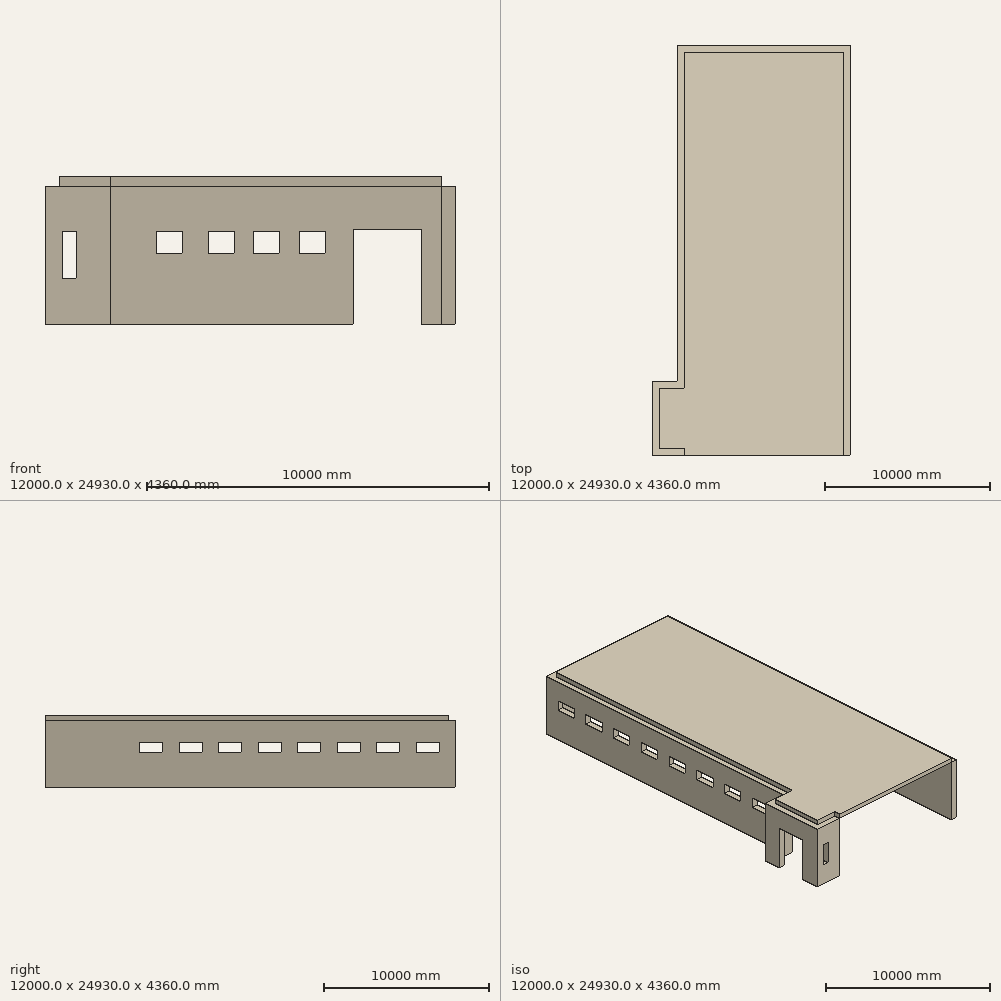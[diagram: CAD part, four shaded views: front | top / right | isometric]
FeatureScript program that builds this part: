
annotation { "Feature Type Name" : "Feature", "Feature Type Description" : "" }
export const myFeature = defineFeature(function(context is Context, id is Id, definition is map)
    precondition{}
    {
        {
            var Q0;
            Q0=qCreatedBy(makeId("Top.planeOp"),FACE);
            var sketch = newSketch(context, id + "F0", { "sketchPlane" : qUnion([Q0])});
            skLineSegment(sketch, "E0", {"start": v(0, 0) * mm, "end": v(0, 24930) * mm});
            skLineSegment(sketch, "E1", {"start": v(0, 24930) * mm, "end": v(-10500, 24930) * mm});
            skLineSegment(sketch, "E2", {"start": v(-10500, 24930) * mm, "end": v(-10500, 4500) * mm});
            skLineSegment(sketch, "E3", {"start": v(-10500, 4500) * mm, "end": v(-12000, 4500) * mm});
            skLineSegment(sketch, "E4", {"start": v(-12000, 4500) * mm, "end": v(-12000, 0) * mm});
            skLineSegment(sketch, "E5.0", {"start": v(-11585, 4085) * mm, "end": v(-11585, 415) * mm});
            skLineSegment(sketch, "E5.1", {"start": v(-10085, 4085) * mm, "end": v(-11585, 4085) * mm});
            skLineSegment(sketch, "E5.2", {"start": v(-10085, 24515) * mm, "end": v(-10085, 4085) * mm});
            skLineSegment(sketch, "E5.3", {"start": v(-415, 24515) * mm, "end": v(-10085, 24515) * mm});
            skLineSegment(sketch, "E5.4", {"start": v(-415, 0) * mm, "end": v(-415, 24515) * mm});
            skLineSegment(sketch, "E6", {"start": v(-12000, 0) * mm, "end": v(-10085, 0) * mm});
            skLineSegment(sketch, "E7", {"start": v(-11585, 415) * mm, "end": v(-10085, 415) * mm});
            skLineSegment(sketch, "E8", {"start": v(-10085, 415) * mm, "end": v(-10085, 0) * mm});
            skLineSegment(sketch, "E9", {"start": v(-415, 0) * mm, "end": v(0, 0) * mm});
            skSolve(sketch);
        }
        {
            var Q0;
            Q0 = qSketchRegion(id + "F0", true);
            extrude(context, id + "F1", {"entities" : qUnion([Q0]), "depth" : 4060 * mm});
        }
        {
            var Q0;
            Q0=makeQuery(id+"F1.opExtrude","SWEPT_FACE",FACE,{"disambiguationData":[OSD([sQuery(id+"F0.wireOp",EDGE,"E2")])]});
            var sketch = newSketch(context, id + "F2", { "sketchPlane" : qUnion([Q0])});
            skLineSegment(sketch, "E10.rect.bottom", {"start": v(-22530, 2100) * mm, "end": v(-23930, 2100) * mm});
            skLineSegment(sketch, "E10.rect.top", {"start": v(-22530, 2750) * mm, "end": v(-23930, 2750) * mm});
            skLineSegment(sketch, "E10.rect.left", {"start": v(-22530, 2100) * mm, "end": v(-22530, 2750) * mm});
            skLineSegment(sketch, "E10.rect.right", {"start": v(-23930, 2100) * mm, "end": v(-23930, 2750) * mm});
            skPoint(sketch, "E10.rect.middle", {"position": v(-23230, 2425) * mm});
            skLineSegment(sketch, "E11.rect.bottom", {"start": v(-20130, 2100) * mm, "end": v(-21530, 2100) * mm});
            skLineSegment(sketch, "E11.rect.top", {"start": v(-20130, 2750) * mm, "end": v(-21530, 2750) * mm});
            skLineSegment(sketch, "E11.rect.left", {"start": v(-20130, 2100) * mm, "end": v(-20130, 2750) * mm});
            skLineSegment(sketch, "E11.rect.right", {"start": v(-21530, 2100) * mm, "end": v(-21530, 2750) * mm});
            skPoint(sketch, "E11.rect.middle", {"position": v(-20830, 2425) * mm});
            skLineSegment(sketch, "E12.rect.bottom", {"start": v(-17730, 2100) * mm, "end": v(-19130, 2100) * mm});
            skLineSegment(sketch, "E12.rect.top", {"start": v(-17730, 2750) * mm, "end": v(-19130, 2750) * mm});
            skLineSegment(sketch, "E12.rect.left", {"start": v(-17730, 2100) * mm, "end": v(-17730, 2750) * mm});
            skLineSegment(sketch, "E12.rect.right", {"start": v(-19130, 2100) * mm, "end": v(-19130, 2750) * mm});
            skPoint(sketch, "E12.rect.middle", {"position": v(-18430, 2425) * mm});
            skLineSegment(sketch, "E13.rect.bottom", {"start": v(-15330, 2100) * mm, "end": v(-16730, 2100) * mm});
            skLineSegment(sketch, "E13.rect.top", {"start": v(-15330, 2750) * mm, "end": v(-16730, 2750) * mm});
            skLineSegment(sketch, "E13.rect.left", {"start": v(-15330, 2100) * mm, "end": v(-15330, 2750) * mm});
            skLineSegment(sketch, "E13.rect.right", {"start": v(-16730, 2100) * mm, "end": v(-16730, 2750) * mm});
            skPoint(sketch, "E13.rect.middle", {"position": v(-16030, 2425) * mm});
            skLineSegment(sketch, "E14.rect.bottom", {"start": v(-12930, 2100) * mm, "end": v(-14330, 2100) * mm});
            skLineSegment(sketch, "E14.rect.top", {"start": v(-12930, 2750) * mm, "end": v(-14330, 2750) * mm});
            skLineSegment(sketch, "E14.rect.left", {"start": v(-12930, 2100) * mm, "end": v(-12930, 2750) * mm});
            skLineSegment(sketch, "E14.rect.right", {"start": v(-14330, 2100) * mm, "end": v(-14330, 2750) * mm});
            skPoint(sketch, "E14.rect.middle", {"position": v(-13630, 2425) * mm});
            skLineSegment(sketch, "E15.rect.bottom", {"start": v(-10530, 2100) * mm, "end": v(-11930, 2100) * mm});
            skLineSegment(sketch, "E15.rect.top", {"start": v(-10530, 2750) * mm, "end": v(-11930, 2750) * mm});
            skLineSegment(sketch, "E15.rect.left", {"start": v(-10530, 2100) * mm, "end": v(-10530, 2750) * mm});
            skLineSegment(sketch, "E15.rect.right", {"start": v(-11930, 2100) * mm, "end": v(-11930, 2750) * mm});
            skPoint(sketch, "E15.rect.middle", {"position": v(-11230, 2425) * mm});
            skLineSegment(sketch, "E16.rect.bottom", {"start": v(-8130, 2100) * mm, "end": v(-9530, 2100) * mm});
            skLineSegment(sketch, "E16.rect.top", {"start": v(-8130, 2750) * mm, "end": v(-9530, 2750) * mm});
            skLineSegment(sketch, "E16.rect.left", {"start": v(-8130, 2100) * mm, "end": v(-8130, 2750) * mm});
            skLineSegment(sketch, "E16.rect.right", {"start": v(-9530, 2100) * mm, "end": v(-9530, 2750) * mm});
            skPoint(sketch, "E16.rect.middle", {"position": v(-8830, 2425) * mm});
            skLineSegment(sketch, "E17.rect.bottom", {"start": v(-5730, 2100) * mm, "end": v(-7130, 2100) * mm});
            skLineSegment(sketch, "E17.rect.top", {"start": v(-5730, 2750) * mm, "end": v(-7130, 2750) * mm});
            skLineSegment(sketch, "E17.rect.left", {"start": v(-5730, 2100) * mm, "end": v(-5730, 2750) * mm});
            skLineSegment(sketch, "E17.rect.right", {"start": v(-7130, 2100) * mm, "end": v(-7130, 2750) * mm});
            skPoint(sketch, "E17.rect.middle", {"position": v(-6430, 2425) * mm});
            skSolve(sketch);
        }
        {
            var Q0;
            Q0 = qSketchRegion(id + "F2", true);
            extrude(context, id + "F3", {"entities" : qUnion([Q0]), "operationType" : NewBodyOperationType.REMOVE, "endBound" : BoundingType.THROUGH_ALL, "oppositeDirection" : true, "depth" : 5000 * mm});
        }
        {
            var Q0;
            Q0=makeQuery(id+"F1.opExtrude","SWEPT_FACE",FACE,{"disambiguationData":[OSD([sQuery(id+"F0.wireOp",EDGE,"E6")])]});
            var sketch = newSketch(context, id + "F4", { "sketchPlane" : qUnion([Q0])});
            skLineSegment(sketch, "E18.rect.bottom", {"start": v(-11100, 1350) * mm, "end": v(-11500, 1350) * mm});
            skLineSegment(sketch, "E18.rect.top", {"start": v(-11100, 2750) * mm, "end": v(-11500, 2750) * mm});
            skLineSegment(sketch, "E18.rect.left", {"start": v(-11100, 1350) * mm, "end": v(-11100, 2750) * mm});
            skLineSegment(sketch, "E18.rect.right", {"start": v(-11500, 1350) * mm, "end": v(-11500, 2750) * mm});
            skPoint(sketch, "E18.rect.middle", {"position": v(-11300, 2050) * mm});
            skSolve(sketch);
        }
        {
            var Q0;
            Q0 = qSketchRegion(id + "F4", true);
            extrude(context, id + "F5", {"entities" : qUnion([Q0]), "operationType" : NewBodyOperationType.REMOVE, "endBound" : BoundingType.THROUGH_ALL, "oppositeDirection" : true, "depth" : 25 * mm});
        }
        {
            var Q0;
            Q0=makeQuery(id+"F1.opExtrude","SWEPT_FACE",FACE,{"disambiguationData":[OSD([sQuery(id+"F0.wireOp",EDGE,"E1")])]});
            var sketch = newSketch(context, id + "F6", { "sketchPlane" : qUnion([Q0])});
            skLineSegment(sketch, "E19.bottom", {"start": v(8754.62, 2100) * mm, "end": v(7994.62, 2100) * mm});
            skLineSegment(sketch, "E19.top", {"start": v(8754.62, 2750) * mm, "end": v(7994.62, 2750) * mm});
            skLineSegment(sketch, "E19.left", {"start": v(8754.62, 2100) * mm, "end": v(8754.62, 2750) * mm});
            skLineSegment(sketch, "E19.right", {"start": v(7994.62, 2100) * mm, "end": v(7994.62, 2750) * mm});
            skLineSegment(sketch, "E20.bottom", {"start": v(7234.62, 2100) * mm, "end": v(6474.62, 2100) * mm});
            skLineSegment(sketch, "E20.top", {"start": v(7234.62, 2750) * mm, "end": v(6474.62, 2750) * mm});
            skLineSegment(sketch, "E20.left", {"start": v(7234.62, 2100) * mm, "end": v(7234.62, 2750) * mm});
            skLineSegment(sketch, "E20.right", {"start": v(6474.62, 2100) * mm, "end": v(6474.62, 2750) * mm});
            skLineSegment(sketch, "E21.bottom", {"start": v(5916.25, 2100) * mm, "end": v(5156.25, 2100) * mm});
            skLineSegment(sketch, "E21.top", {"start": v(5916.25, 2750) * mm, "end": v(5156.25, 2750) * mm});
            skLineSegment(sketch, "E21.left", {"start": v(5916.25, 2100) * mm, "end": v(5916.25, 2750) * mm});
            skLineSegment(sketch, "E21.right", {"start": v(5156.25, 2100) * mm, "end": v(5156.25, 2750) * mm});
            skLineSegment(sketch, "E22.bottom", {"start": v(4551.35, 2100) * mm, "end": v(3791.35, 2100) * mm});
            skLineSegment(sketch, "E22.top", {"start": v(4551.35, 2750) * mm, "end": v(3791.35, 2750) * mm});
            skLineSegment(sketch, "E22.left", {"start": v(4551.35, 2100) * mm, "end": v(4551.35, 2750) * mm});
            skLineSegment(sketch, "E22.right", {"start": v(3791.35, 2100) * mm, "end": v(3791.35, 2750) * mm});
            skLineSegment(sketch, "E23.bottom", {"start": v(2999.51, 0) * mm, "end": v(999.51, 0) * mm});
            skLineSegment(sketch, "E23.top", {"start": v(2999.51, 2800) * mm, "end": v(999.51, 2800) * mm});
            skLineSegment(sketch, "E23.left", {"start": v(2999.51, 0) * mm, "end": v(2999.51, 2800) * mm});
            skLineSegment(sketch, "E23.right", {"start": v(999.51, 0) * mm, "end": v(999.51, 2800) * mm});
            skSolve(sketch);
        }
        {
            var Q0;
            Q0=makeQuery(id+"F6.imprint","IMPRINT",FACE,{"disambiguationData":[TD([[makeQuery(id+"F6.imprint","IMPRINT",EDGE,{"derivedFrom":sQuery(id+"F6.wireOp",EDGE,"E23.bottom")}),1.0]])]});
            var Q1;
            Q1=makeQuery(id+"F6.imprint","IMPRINT",FACE,{"disambiguationData":[TD([[makeQuery(id+"F6.imprint","IMPRINT",EDGE,{"derivedFrom":sQuery(id+"F6.wireOp",EDGE,"E22.bottom")}),-1.0]])]});
            var Q2;
            Q2=makeQuery(id+"F6.imprint","IMPRINT",FACE,{"disambiguationData":[TD([[makeQuery(id+"F6.imprint","IMPRINT",EDGE,{"derivedFrom":sQuery(id+"F6.wireOp",EDGE,"E21.bottom")}),-1.0]])]});
            var Q3;
            Q3=makeQuery(id+"F6.imprint","IMPRINT",FACE,{"disambiguationData":[TD([[makeQuery(id+"F6.imprint","IMPRINT",EDGE,{"derivedFrom":sQuery(id+"F6.wireOp",EDGE,"E20.bottom")}),-1.0]])]});
            var Q4;
            Q4=makeQuery(id+"F6.imprint","IMPRINT",FACE,{"disambiguationData":[TD([[makeQuery(id+"F6.imprint","IMPRINT",EDGE,{"derivedFrom":sQuery(id+"F6.wireOp",EDGE,"E19.bottom")}),-1.0]])]});
            extrude(context, id + "F7", {"entities" : qUnion([Q0, Q1, Q2, Q3, Q4]), "operationType" : NewBodyOperationType.REMOVE, "endBound" : BoundingType.THROUGH_ALL, "oppositeDirection" : true, "depth" : 25 * mm});
        }
        {
            var Q0;
            Q0=makeQuery(id+"F1.opExtrude","SWEPT_FACE",FACE,{"disambiguationData":[OSD([sQuery(id+"F0.wireOp",EDGE,"E4")])]});
            var sketch = newSketch(context, id + "F8", { "sketchPlane" : qUnion([Q0])});
            skLineSegment(sketch, "E24.bottom", {"start": v(-1300, 0) * mm, "end": v(-3300, 0) * mm});
            skLineSegment(sketch, "E24.top", {"start": v(-1300, 2800) * mm, "end": v(-3300, 2800) * mm});
            skLineSegment(sketch, "E24.left", {"start": v(-1300, 0) * mm, "end": v(-1300, 2800) * mm});
            skLineSegment(sketch, "E24.right", {"start": v(-3300, 0) * mm, "end": v(-3300, 2800) * mm});
            skSolve(sketch);
        }
        {
            var Q0;
            Q0=makeQuery(id+"F8.imprint","IMPRINT",FACE,{"disambiguationData":[TD([[makeQuery(id+"F8.imprint","IMPRINT",EDGE,{"derivedFrom":sQuery(id+"F8.wireOp",EDGE,"E24.bottom")}),1.0]])]});
            extrude(context, id + "F9", {"entities" : qUnion([Q0]), "operationType" : NewBodyOperationType.REMOVE, "oppositeDirection" : true, "depth" : 1000 * mm});
        }
        {
            var Q0;
            Q0=makeQuery(id+"F1.opExtrude","CAP_FACE",FACE,{"disambiguationData":[OSD([sQuery(id+"F0.wireOp",EDGE,"E0"),sQuery(id+"F0.wireOp",EDGE,"E1"),sQuery(id+"F0.wireOp",EDGE,"E2"),sQuery(id+"F0.wireOp",EDGE,"E3"),sQuery(id+"F0.wireOp",EDGE,"E4"),sQuery(id+"F0.wireOp",EDGE,"E5.0"),sQuery(id+"F0.wireOp",EDGE,"E5.1"),sQuery(id+"F0.wireOp",EDGE,"E5.2"),sQuery(id+"F0.wireOp",EDGE,"E5.3"),sQuery(id+"F0.wireOp",EDGE,"E5.4"),sQuery(id+"F0.wireOp",EDGE,"E6"),sQuery(id+"F0.wireOp",EDGE,"E7"),sQuery(id+"F0.wireOp",EDGE,"E8"),sQuery(id+"F0.wireOp",EDGE,"E9")])],"isStart":false});
            var sketch = newSketch(context, id + "F10", { "sketchPlane" : qUnion([Q0])});
            skLineSegment(sketch, "E25.0", {"start": v(-10085, 24515) * mm, "end": v(-10085, 4085) * mm});
            skLineSegment(sketch, "E25.1", {"start": v(-415, 0) * mm, "end": v(-415, 24515) * mm});
            skLineSegment(sketch, "E25.2", {"start": v(-415, 24515) * mm, "end": v(-10085, 24515) * mm});
            skLineSegment(sketch, "E25.3", {"start": v(-10085, 4085) * mm, "end": v(-11585, 4085) * mm});
            skLineSegment(sketch, "E25.4", {"start": v(-11585, 4085) * mm, "end": v(-11585, 415) * mm});
            skLineSegment(sketch, "E25.5", {"start": v(-11585, 415) * mm, "end": v(-10085, 415) * mm});
            skLineSegment(sketch, "E25.6", {"start": v(-10085, 415) * mm, "end": v(-10085, 0) * mm});
            skLineSegment(sketch, "E26", {"start": v(-10085, 0) * mm, "end": v(-415, 0) * mm});
            skSolve(sketch);
        }
        {
            var Q0;
            Q0=makeQuery(id+"F10.imprint","IMPRINT",FACE,{"disambiguationData":[TD([[makeQuery(id+"F10.imprint","IMPRINT",EDGE,{"derivedFrom":sQuery(id+"F10.wireOp",EDGE,"E25.0")}),1.0]])]});
            extrude(context, id + "F11", {"entities" : qUnion([Q0]), "depth" : 300 * mm});
        }
    });
